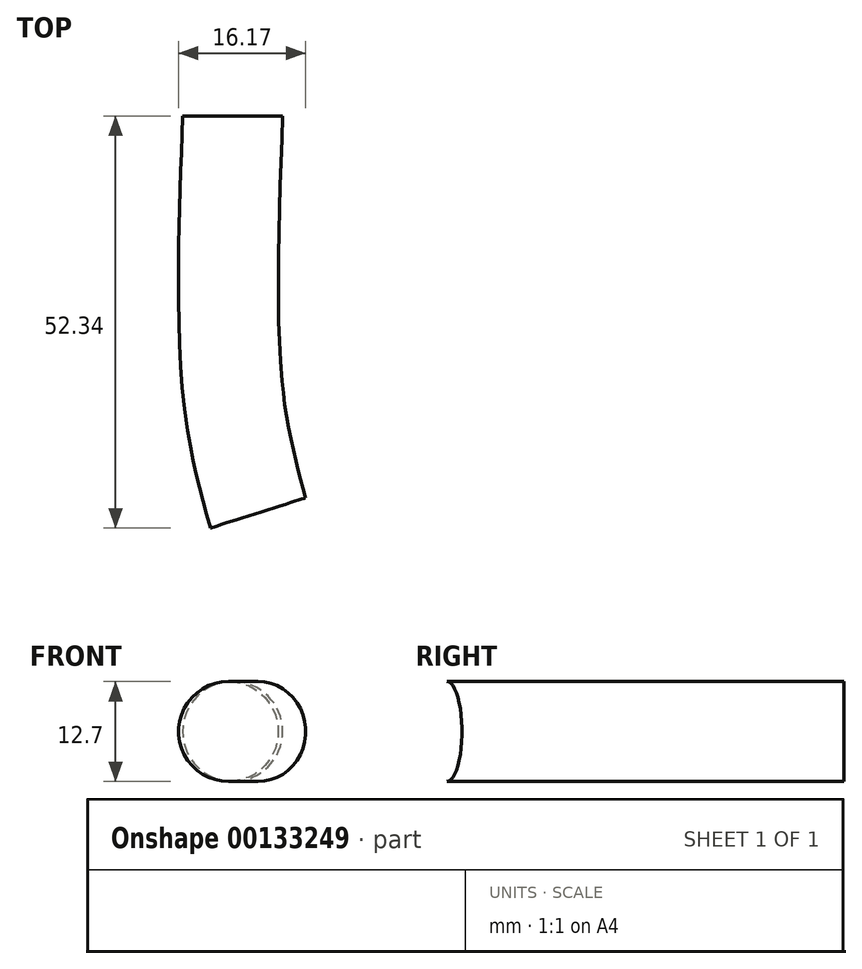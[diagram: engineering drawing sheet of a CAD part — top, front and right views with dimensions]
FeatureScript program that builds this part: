
annotation { "Feature Type Name" : "Feature", "Feature Type Description" : "" }
export const myFeature = defineFeature(function(context is Context, id is Id, definition is map)
    precondition{}
    {
        {
            var Q0;
            Q0=qCreatedBy(makeId("Front.planeOp"),FACE);
            var sketch = newSketch(context, id + "F0", { "sketchPlane" : qUnion([Q0])});
            skCircle(sketch, "E0", {"center": v(0, 0) * mm, "radius": 6.35 * mm});
            skSolve(sketch);
        }
        {
            var Q0;
            Q0=qCreatedBy(makeId("Top.planeOp"),FACE);
            var sketch = newSketch(context, id + "F1", { "sketchPlane" : qUnion([Q0])});
            skFitSpline(sketch, "E1", {"points": [v(0, 0) * mm, v(0, -34.82) * mm, v(3.23, -50.42) * mm], "startDerivative": vector(-2.39, -64.26) * mm, "endDerivative": vector(9.61, -34.68) * mm});
            skSolve(sketch);
        }
        {
            var Q0;
            Q0=makeQuery(id+"F0.imprint","IMPRINT",FACE,{"disambiguationData":[TD([[makeQuery(id+"F0.imprint","IMPRINT",EDGE,{"derivedFrom":sQuery(id+"F0.wireOp",EDGE,"E0")}),1.0]])]});
            var Q1;
            Q1 = qConstructionFilter(qBodyType(qCreatedBy(id + "F1" ,EDGE), BodyType.WIRE), ConstructionObject.NO);
            sweep(context, id + "F2", {"profiles" : qUnion([Q0]), "path" : qUnion([Q1])});
        }
    });
